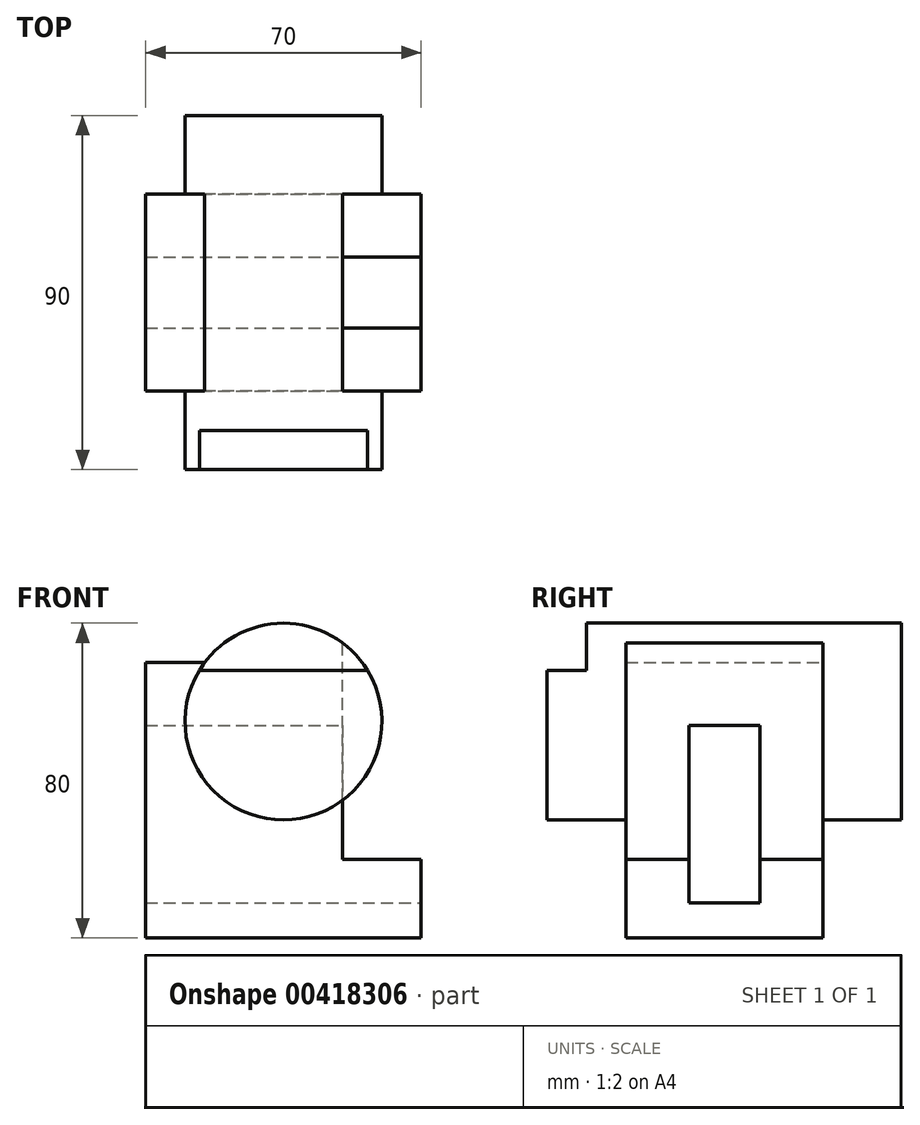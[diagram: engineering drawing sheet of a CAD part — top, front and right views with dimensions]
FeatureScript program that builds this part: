
annotation { "Feature Type Name" : "Feature", "Feature Type Description" : "" }
export const myFeature = defineFeature(function(context is Context, id is Id, definition is map)
    precondition{}
    {
        {
            var Q0;
            Q0=qCreatedBy(makeId("Top.planeOp"),FACE);
            var sketch = newSketch(context, id + "F0", { "sketchPlane" : qUnion([Q0])});
            skLineSegment(sketch, "E0.bottom", {"start": v(-35, 25) * mm, "end": v(35, 25) * mm});
            skLineSegment(sketch, "E0.top", {"start": v(-35, -25) * mm, "end": v(35, -25) * mm});
            skLineSegment(sketch, "E0.left", {"start": v(-35, 25) * mm, "end": v(-35, -25) * mm});
            skLineSegment(sketch, "E0.right", {"start": v(35, 25) * mm, "end": v(35, -25) * mm});
            skPoint(sketch, "E0.middle", {"position": v(0, 0) * mm});
            skSolve(sketch);
        }
        {
            var Q0;
            Q0 = qSketchRegion(id + "F0", true);
            extrude(context, id + "F1", {"entities" : qUnion([Q0]), "depth" : 70 * mm});
        }
        {
            var Q0;
            Q0=makeQuery(id+"F1.opExtrude","SWEPT_FACE",FACE,{"disambiguationData":[OSD([sQuery(id+"F0.wireOp",EDGE,"E0.top")])]});
            var sketch = newSketch(context, id + "F2", { "sketchPlane" : qUnion([Q0])});
            skCircle(sketch, "E1", {"center": v(0, 55) * mm, "radius": 25 * mm});
            skSolve(sketch);
        }
        {
            var Q0;
            Q0 = qSketchRegion(id + "F2", true);
            extrude(context, id + "F3", {"entities" : qUnion([Q0]), "operationType" : NewBodyOperationType.ADD, "depth" : 20 * mm, "hasSecondDirection" : true, "secondDirectionOppositeDirection" : true, "secondDirectionDepth" : 70 * mm});
        }
        {
            var Q0;
            Q0=makeQuery(id+"F1.opExtrude","SWEPT_FACE",FACE,{"disambiguationData":[OSD([sQuery(id+"F0.wireOp",EDGE,"E0.right")])]});
            var sketch = newSketch(context, id + "F4", { "sketchPlane" : qUnion([Q0])});
            skLineSegment(sketch, "E2.bottom", {"start": v(-9, 9) * mm, "end": v(9, 9) * mm});
            skLineSegment(sketch, "E2.top", {"start": v(-9, 54) * mm, "end": v(9, 54) * mm});
            skLineSegment(sketch, "E2.left", {"start": v(-9, 9) * mm, "end": v(-9, 54) * mm});
            skLineSegment(sketch, "E2.right", {"start": v(9, 9) * mm, "end": v(9, 54) * mm});
            skSolve(sketch);
        }
        {
            var Q0;
            Q0 = qSketchRegion(id + "F4", true);
            extrude(context, id + "F5", {"entities" : qUnion([Q0]), "operationType" : NewBodyOperationType.REMOVE, "endBound" : BoundingType.THROUGH_ALL, "oppositeDirection" : true, "depth" : 25 * mm});
        }
        {
            var Q0;
            Q0=makeQuery(id+"F3.opExtrude","CAP_FACE",FACE,{"disambiguationData":[OSD([sQuery(id+"F2.wireOp",EDGE,"E1")])],"isStart":false});
            var sketch = newSketch(context, id + "F6", { "sketchPlane" : qUnion([Q0])});
            skLineSegment(sketch, "E3.bottom", {"start": v(-25, 88) * mm, "end": v(25, 88) * mm});
            skLineSegment(sketch, "E3.top", {"start": v(-25, 68) * mm, "end": v(25, 68) * mm});
            skLineSegment(sketch, "E3.left", {"start": v(-25, 88) * mm, "end": v(-25, 68) * mm});
            skLineSegment(sketch, "E3.right", {"start": v(25, 88) * mm, "end": v(25, 68) * mm});
            skSolve(sketch);
        }
        {
            var Q0;
            Q0 = qSketchRegion(id + "F6", true);
            extrude(context, id + "F7", {"entities" : qUnion([Q0]), "operationType" : NewBodyOperationType.REMOVE, "oppositeDirection" : true, "depth" : 10 * mm});
        }
        {
            var Q0;
            Q0=makeQuery(id+"F1.opExtrude","SWEPT_FACE",FACE,{"disambiguationData":[OSD([sQuery(id+"F0.wireOp",EDGE,"E0.right")])]});
            var sketch = newSketch(context, id + "F8", { "sketchPlane" : qUnion([Q0])});
            skLineSegment(sketch, "E4.bottom", {"start": v(-25, 20) * mm, "end": v(25, 20) * mm});
            skLineSegment(sketch, "E4.top", {"start": v(-25, 120) * mm, "end": v(25, 120) * mm});
            skLineSegment(sketch, "E4.left", {"start": v(-25, 20) * mm, "end": v(-25, 120) * mm});
            skLineSegment(sketch, "E4.right", {"start": v(25, 20) * mm, "end": v(25, 120) * mm});
            skSolve(sketch);
        }
        {
            var Q0;
            Q0 = qSketchRegion(id + "F8", true);
            extrude(context, id + "F9", {"entities" : qUnion([Q0]), "operationType" : NewBodyOperationType.REMOVE, "oppositeDirection" : true, "depth" : 20 * mm});
        }
    });
